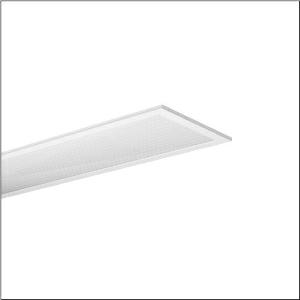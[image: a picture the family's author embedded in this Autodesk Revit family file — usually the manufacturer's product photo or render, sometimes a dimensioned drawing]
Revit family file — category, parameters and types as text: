
# Revit family: apollon_r__21_linear_51mq17wd2612_dc58
name_source: partatom
category: Lighting Fixtures
units: mm (PartAtom-declared; Revit-internal decimal feet)

## family parameters
Cut with Voids When Loaded = No
Host = Face
Light Source = No
Part Type = Normal
Room Calculation Point = No
Round Connector Dimension = Use Diameter
Shared = No

## types (1)
- Apollon® 21 linear (1 x LED, 6900 lm, 60 W, 6500K)
    Apparent Load = 60 VA
    CIE Flux Codes = 61 87 97 100 100
    Color Rendering = 80
    Color Temperature = 6500K
    Default Elevation = 1800 mm
    Description = Apollon® 21 linear, office luminaire, primary optical cover: micro prismatic cover, CAT 2 (L<= 3000cd/m²), light emission: direct distribution, primary light characteristic: symmetric, installation type: lay-in mounting, LED, rated luminous flux: 6.900lm, luminous efficacy: 115lm/W, light colour: 865, colour temperature: 6500K, with terminal, 5-pole, mains connection: 220..240V, AC, 50/60Hz, rated input power: 60W, housing, of aluminium, coated, pure white, length: 1.545mm, width: 307mm, height: 48mm, housing upper side, of sheet steel, galvanised, protection rating (complete): IP20, protection rating (lamp compartment, on room side): IP50, insulation class (complete): insulation class II (safety insulation), certification: CE, ENEC, packaging unit: 1 piece
    Height = 0 mm  [stored 0 ft]
    Lamp = 1 x LED
    Lamp Light Flux = 6900 lm
    Lamp Power = 60 W
    Lamp count = 1
    Length = 1545 mm
    Luminous efficacy = 115 lm/W
    Manufacturer = Siteco
    ModVariant = No
    Model = 51MQ17WD2612
    Mounting Place = Ceiling
    Mounting Type = Recessed
    Number of Poles = 1
    OnlyDefault = Yes
    Power Factor = 1
    Product Name = Apollon® 21 linear
    Product group = office luminaire | ceiling recessed
    ProductGroupID = 401
    Protection Class = Protection class II
    Protection Degree = IP 20
    RLX_Detail_Level = 1
    RLX_Emergency_Light_Flux = 0 lm
    RLX_Emergency_Type = 0
    RLX_Emergency_Type_DB = No
    RlxData = <blob elided: 17193 chars, md5=e8540f03>
    Socket = socket
    Standby Power = 0 W
    System Light Flux = 6900 lm
    System Power = 60 W
    Type Comments = Product without accessories
    Type Image = l_1291045.jpg
    URL = http://relux.com
    VarID = ---
    Voltage = 0 V
    Weight = 0.00 kg
    Width = 307 mm

note: [stored X ft] marks values corroborated as IEEE doubles in the binary element streams (Revit-internal decimal feet)

## geometry (parser evidence)
native form markers: Blend x4, Sweep x10
no freeform markers — native parametric forms only
